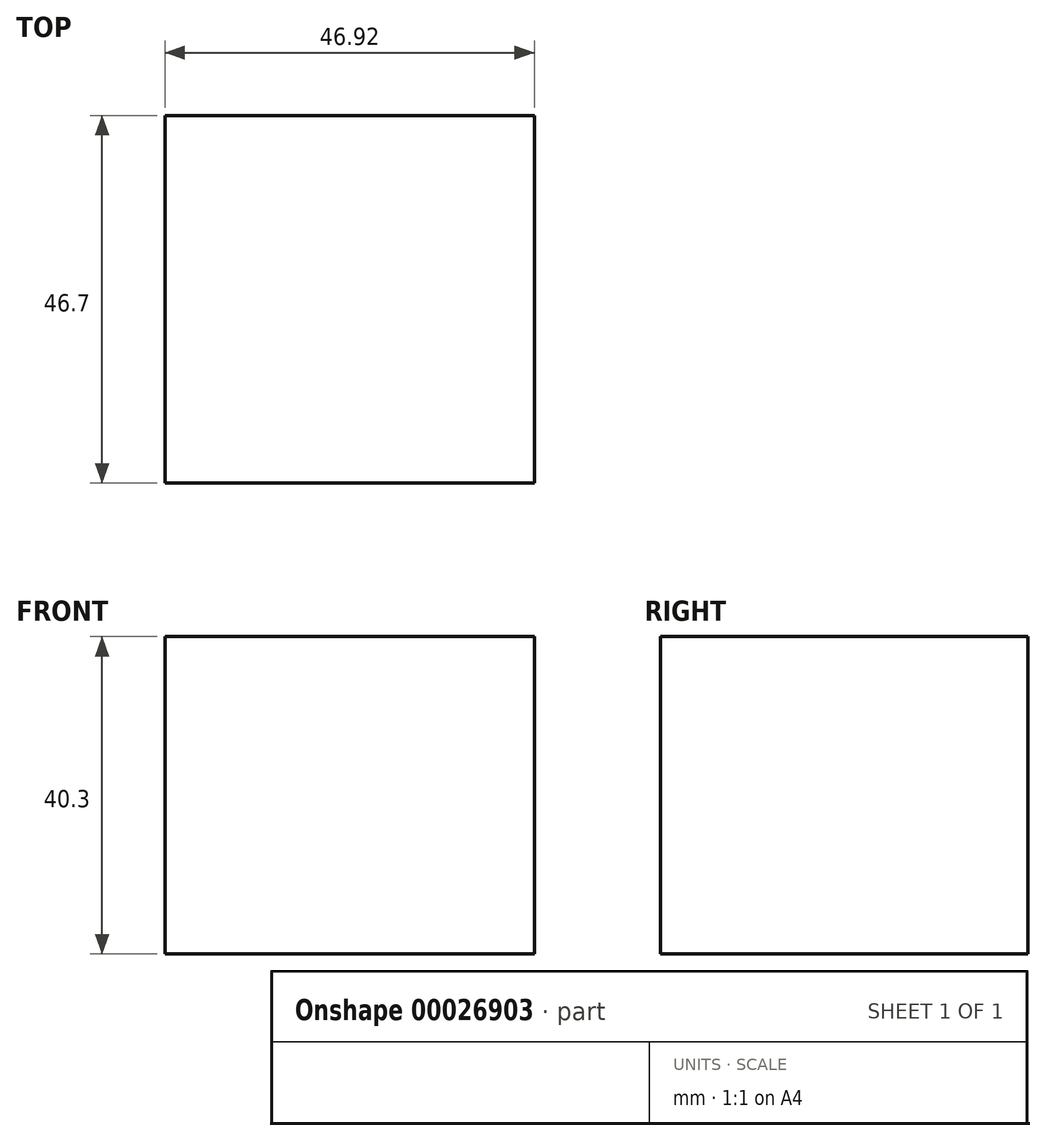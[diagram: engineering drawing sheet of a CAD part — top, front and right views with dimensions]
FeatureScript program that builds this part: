
annotation { "Feature Type Name" : "Feature", "Feature Type Description" : "" }
export const myFeature = defineFeature(function(context is Context, id is Id, definition is map)
    precondition{}
    {
        {
            var Q0;
            Q0=qCreatedBy(makeId("Top.planeOp"),FACE);
            var sketch = newSketch(context, id + "F0", { "sketchPlane" : qUnion([Q0])});
            skLineSegment(sketch, "E0.bottom", {"start": v(23.46, 24.43) * mm, "end": v(-23.46, 24.43) * mm});
            skLineSegment(sketch, "E0.top", {"start": v(23.46, -22.27) * mm, "end": v(-23.46, -22.27) * mm});
            skLineSegment(sketch, "E0.left", {"start": v(23.46, 24.43) * mm, "end": v(23.46, -22.27) * mm});
            skLineSegment(sketch, "E0.right", {"start": v(-23.46, 24.43) * mm, "end": v(-23.46, -22.27) * mm});
            skPoint(sketch, "E0.middle", {"position": v(0, 1.08) * mm});
            skSolve(sketch);
        }
        {
            var Q0;
            Q0=makeQuery(id+"F0.imprint","IMPRINT",FACE,{"disambiguationData":[TD([[makeQuery(id+"F0.imprint","IMPRINT",EDGE,{"derivedFrom":sQuery(id+"F0.wireOp",EDGE,"E0.bottom")}),1.0]])]});
            extrude(context, id + "F1", {"entities" : qUnion([Q0]), "depth" : 40.3 * mm});
        }
    });
